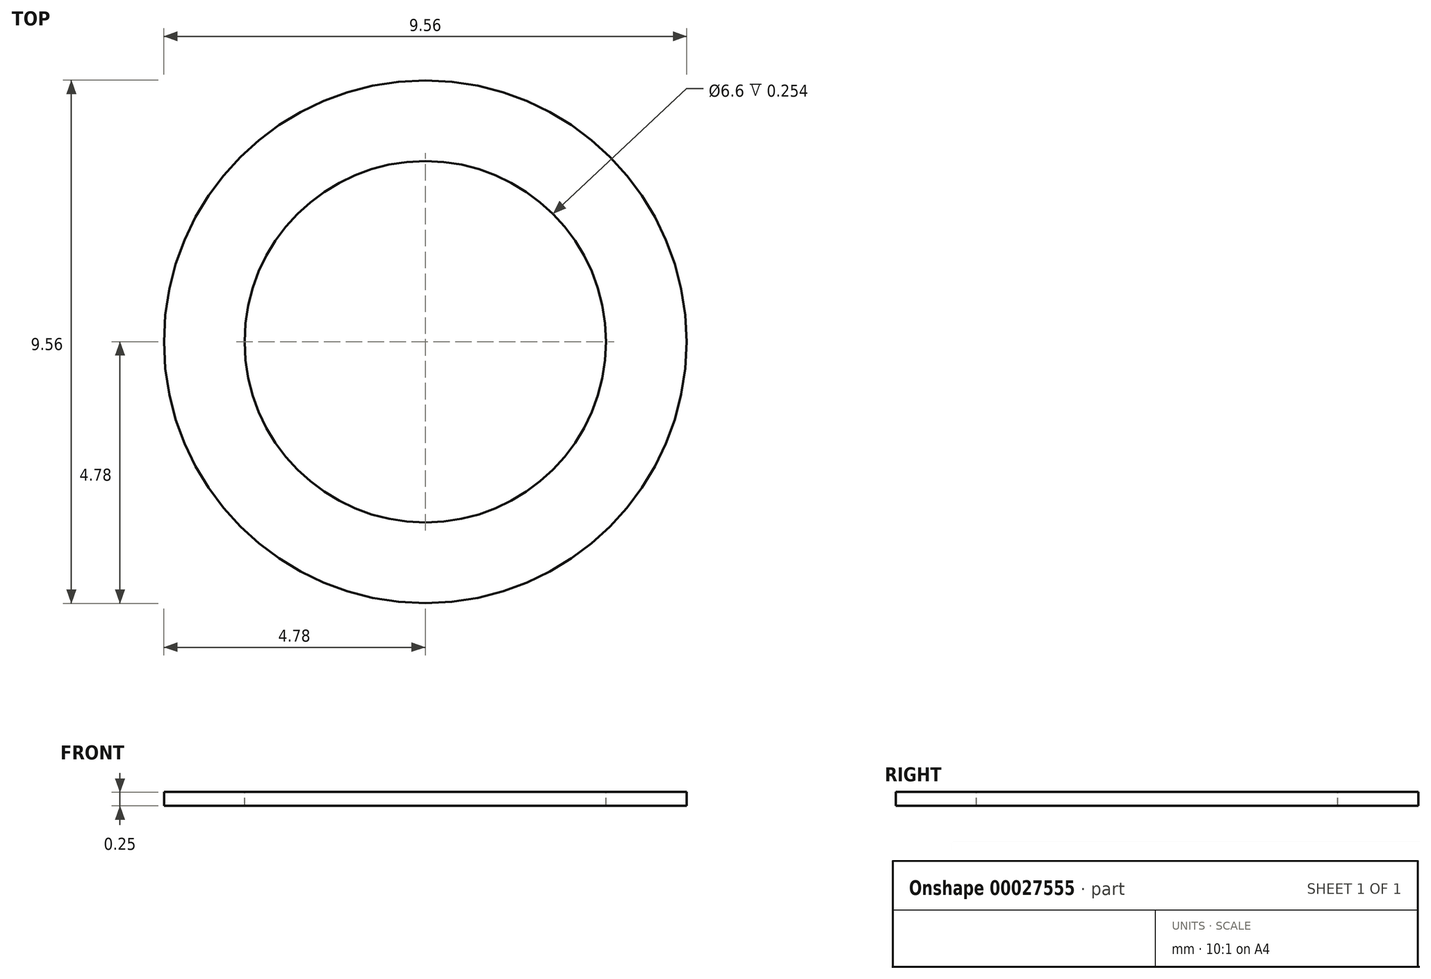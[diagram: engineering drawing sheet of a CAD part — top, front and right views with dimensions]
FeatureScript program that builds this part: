
annotation { "Feature Type Name" : "Feature", "Feature Type Description" : "" }
export const myFeature = defineFeature(function(context is Context, id is Id, definition is map)
    precondition{}
    {
        {
            var Q0;
            Q0=qCreatedBy(makeId("Front.planeOp"),FACE);
            var sketch = newSketch(context, id + "F0", { "sketchPlane" : qUnion([Q0])});
            skLineSegment(sketch, "E0.bottom", {"start": v(3.3, 0) * mm, "end": v(4.78, 0) * mm});
            skLineSegment(sketch, "E0.top", {"start": v(3.3, 0.25) * mm, "end": v(4.78, 0.25) * mm});
            skLineSegment(sketch, "E0.left", {"start": v(3.3, 0) * mm, "end": v(3.3, 0.25) * mm});
            skLineSegment(sketch, "E0.right", {"start": v(4.78, 0) * mm, "end": v(4.78, 0.25) * mm});
            skLineSegment(sketch, "E1", {"start": v(0, 11.08) * mm, "end": v(0, -10.55) * mm, "construction": true});
            skSolve(sketch);
        }
        {
            var Q0;
            Q0 = qSketchRegion(id + "F0", true);
            var Q1;
            Q1=sQuery(id+"F0.wireOp",EDGE,"E1");
            revolve(context, id + "F1", {"entities" : qUnion([Q0]), "axis" : qUnion([Q1]), "revolveType" : RevolveType.FULL});
        }
    });
